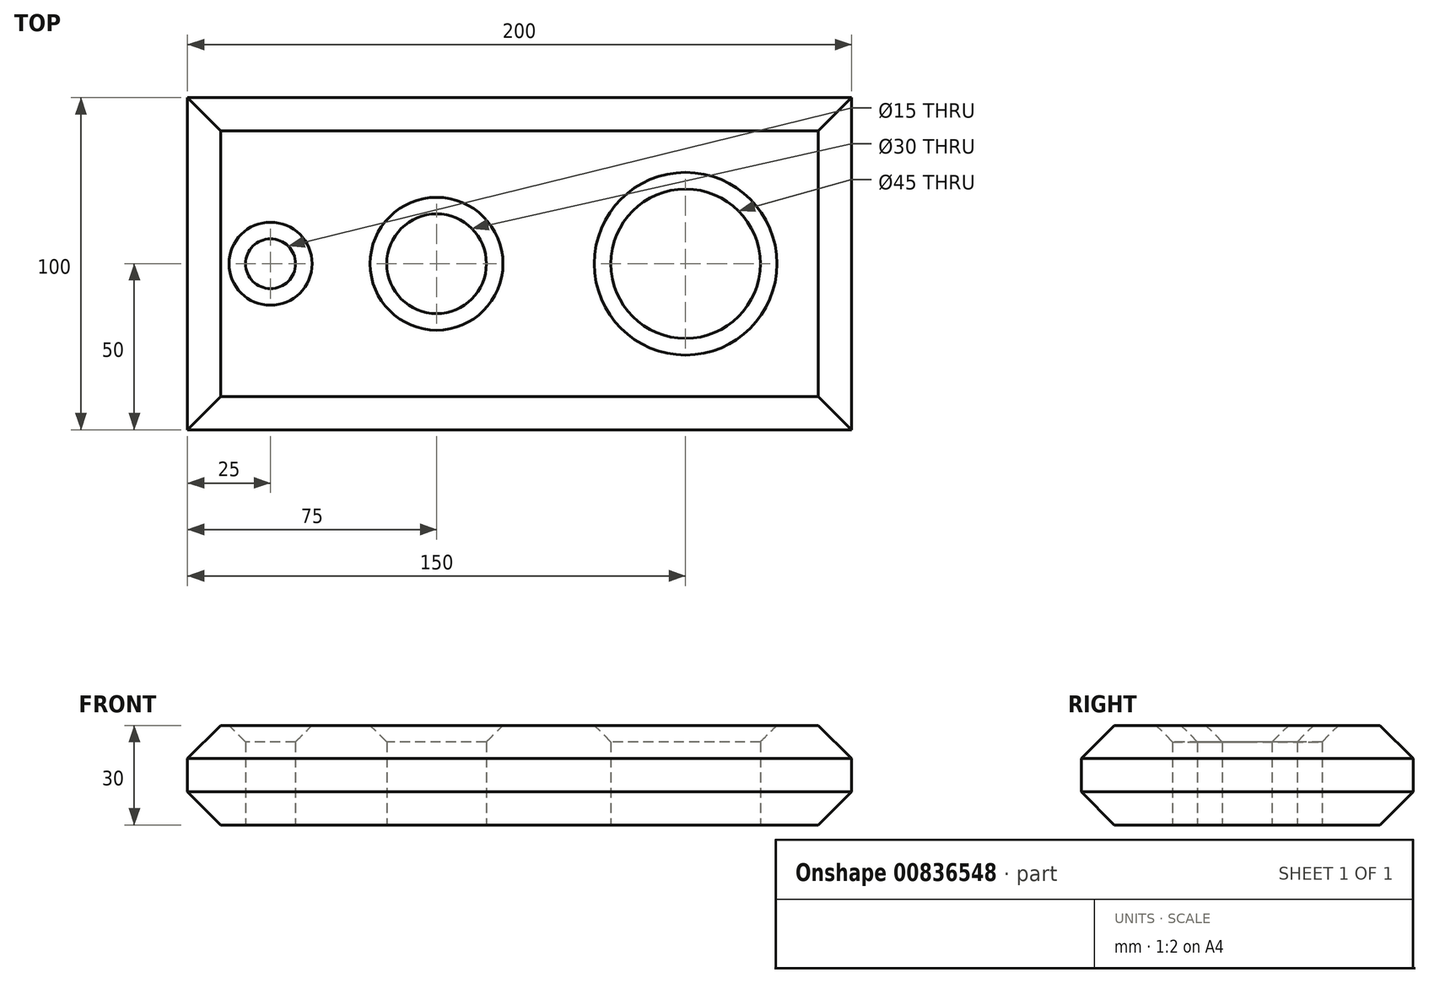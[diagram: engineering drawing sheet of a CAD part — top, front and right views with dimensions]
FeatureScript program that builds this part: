
annotation { "Feature Type Name" : "Feature", "Feature Type Description" : "" }
export const myFeature = defineFeature(function(context is Context, id is Id, definition is map)
    precondition{}
    {
        {
            var Q0;
            Q0=qCreatedBy(makeId("Top.planeOp"),FACE);
            var sketch = newSketch(context, id + "F0", { "sketchPlane" : qUnion([Q0])});
            skLineSegment(sketch, "E0.bottom", {"start": v(100, -50) * mm, "end": v(-100, -50) * mm});
            skLineSegment(sketch, "E0.top", {"start": v(100, 50) * mm, "end": v(-100, 50) * mm});
            skLineSegment(sketch, "E0.left", {"start": v(100, -50) * mm, "end": v(100, 50) * mm});
            skLineSegment(sketch, "E0.right", {"start": v(-100, -50) * mm, "end": v(-100, 50) * mm});
            skPoint(sketch, "E0.middle", {"position": v(0, 0) * mm});
            skCircle(sketch, "E1", {"center": v(-75, 0) * mm, "radius": 7.5 * mm});
            skCircle(sketch, "E2", {"center": v(-25, 0) * mm, "radius": 15 * mm});
            skCircle(sketch, "E3", {"center": v(50, 0) * mm, "radius": 22.5 * mm});
            skSolve(sketch);
        }
        {
            var Q0;
            Q0=makeQuery(id+"F0.imprint","IMPRINT",FACE,{"disambiguationData":[TD([[makeQuery(id+"F0.imprint","IMPRINT",EDGE,{"derivedFrom":sQuery(id+"F0.wireOp",EDGE,"E0.bottom")}),-1.0]])]});
            extrude(context, id + "F1", {"entities" : qUnion([Q0]), "depth" : 30 * mm, "offsetDistance" : 25 * mm});
        }
        {
            var Q0;
            Q0=makeQuery(id+"F1.opExtrude","CAP_EDGE",EDGE,{"disambiguationData":[OSD([sQuery(id+"F0.wireOp",EDGE,"E0.right")])],"isStart":false});
            var Q1;
            Q1=makeQuery(id+"F1.opExtrude","CAP_EDGE",EDGE,{"disambiguationData":[OSD([sQuery(id+"F0.wireOp",EDGE,"E0.top")])],"isStart":false});
            var Q2;
            Q2=makeQuery(id+"F1.opExtrude","CAP_EDGE",EDGE,{"disambiguationData":[OSD([sQuery(id+"F0.wireOp",EDGE,"E0.bottom")])],"isStart":false});
            var Q3;
            Q3=makeQuery(id+"F1.opExtrude","CAP_EDGE",EDGE,{"disambiguationData":[OSD([sQuery(id+"F0.wireOp",EDGE,"E0.left")])],"isStart":false});
            var Q4;
            Q4=makeQuery(id+"F1.opExtrude","CAP_EDGE",EDGE,{"disambiguationData":[OSD([sQuery(id+"F0.wireOp",EDGE,"E0.bottom")])],"isStart":true});
            var Q5;
            Q5=makeQuery(id+"F1.opExtrude","CAP_EDGE",EDGE,{"disambiguationData":[OSD([sQuery(id+"F0.wireOp",EDGE,"E0.right")])],"isStart":true});
            var Q6;
            Q6=makeQuery(id+"F1.opExtrude","CAP_EDGE",EDGE,{"disambiguationData":[OSD([sQuery(id+"F0.wireOp",EDGE,"E0.top")])],"isStart":true});
            var Q7;
            Q7=makeQuery(id+"F1.opExtrude","CAP_EDGE",EDGE,{"disambiguationData":[OSD([sQuery(id+"F0.wireOp",EDGE,"E0.left")])],"isStart":true});
            chamfer(context, id + "F2", {"entities" : qUnion([Q0, Q1, Q2, Q3, Q4, Q5, Q6, Q7]), "width" : 10 * mm, "tangentPropagation" : true});
        }
        {
            var Q0;
            Q0=makeQuery(id+"F1.opExtrude","CAP_EDGE",EDGE,{"disambiguationData":[OSD([sQuery(id+"F0.wireOp",EDGE,"E2")])],"isStart":false});
            var Q1;
            Q1=makeQuery(id+"F1.opExtrude","CAP_EDGE",EDGE,{"disambiguationData":[OSD([sQuery(id+"F0.wireOp",EDGE,"E1")])],"isStart":false});
            var Q2;
            Q2=makeQuery(id+"F1.opExtrude","CAP_EDGE",EDGE,{"disambiguationData":[OSD([sQuery(id+"F0.wireOp",EDGE,"E3")])],"isStart":false});
            chamfer(context, id + "F3", {"entities" : qUnion([Q0, Q1, Q2]), "width" : 5 * mm, "tangentPropagation" : true});
        }
    });
